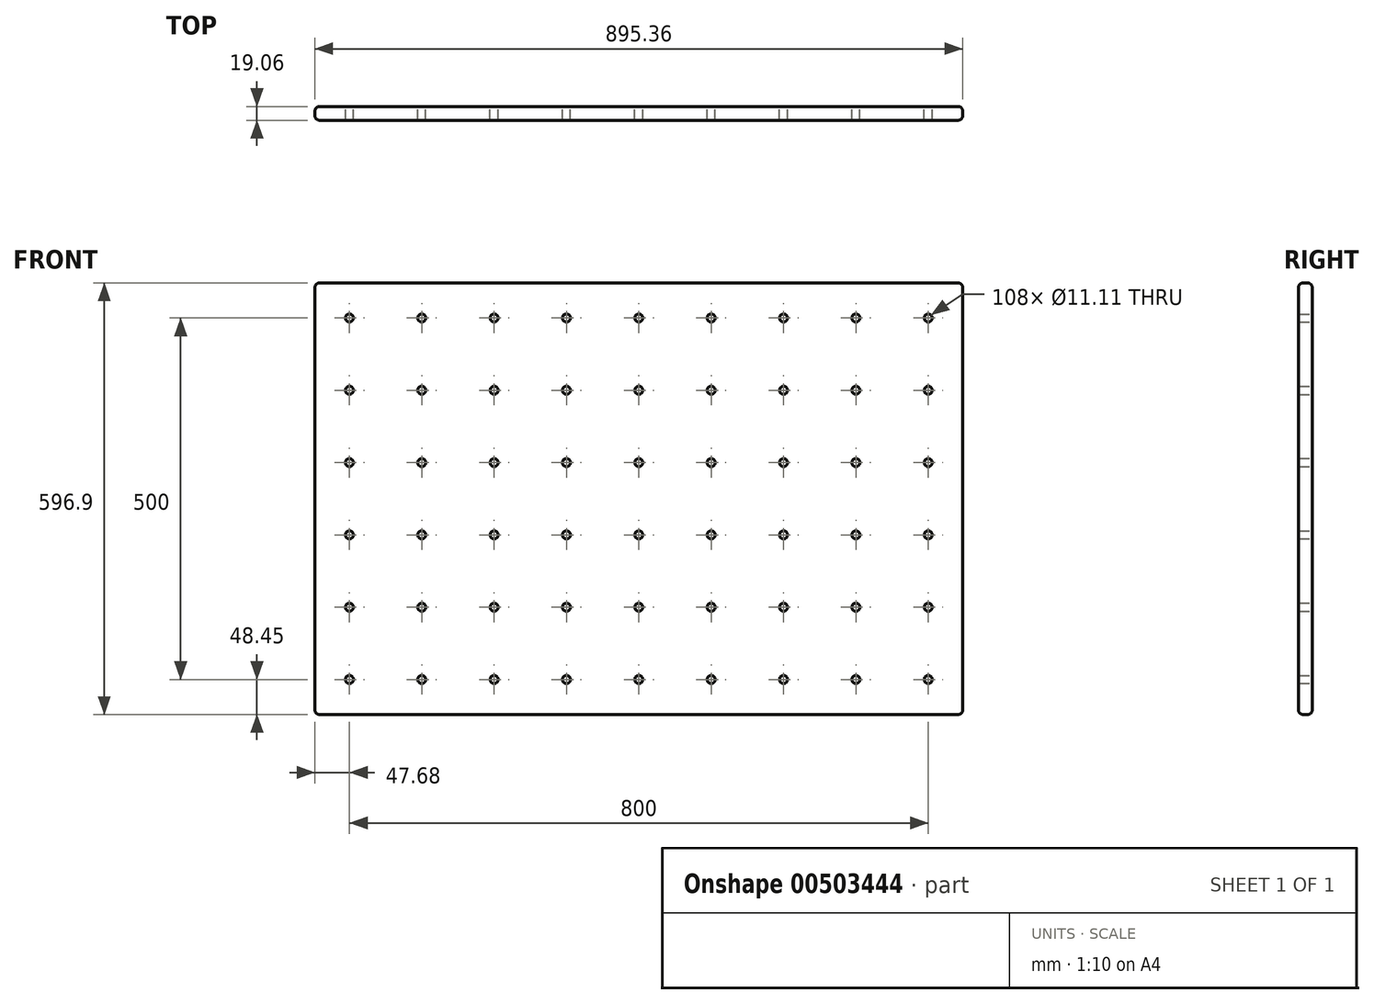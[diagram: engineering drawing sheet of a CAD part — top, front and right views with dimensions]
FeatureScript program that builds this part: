
annotation { "Feature Type Name" : "Feature", "Feature Type Description" : "" }
export const myFeature = defineFeature(function(context is Context, id is Id, definition is map)
    precondition{}
    {
        {
            var Q0;
            Q0=qCreatedBy(makeId("Front.planeOp"),FACE);
            var sketch = newSketch(context, id + "F0", { "sketchPlane" : qUnion([Q0])});
            skLineSegment(sketch, "E0.bottom", {"start": v(-447.68, 298.45) * mm, "end": v(447.68, 298.45) * mm});
            skLineSegment(sketch, "E0.top", {"start": v(-447.68, -298.45) * mm, "end": v(447.67, -298.45) * mm});
            skLineSegment(sketch, "E0.left", {"start": v(-447.68, 298.45) * mm, "end": v(-447.68, -298.45) * mm});
            skLineSegment(sketch, "E0.right", {"start": v(447.68, 298.45) * mm, "end": v(447.67, -298.45) * mm});
            skCircle(sketch, "E1", {"center": v(400, -250) * mm, "radius": 5.56 * mm});
            skCircle(sketch, "E2.0.1.0", {"center": v(400, -150) * mm, "radius": 5.56 * mm});
            skCircle(sketch, "E2.0.2.0", {"center": v(400, -50) * mm, "radius": 5.56 * mm});
            skCircle(sketch, "E2.0.3.0", {"center": v(400, 50) * mm, "radius": 5.56 * mm});
            skCircle(sketch, "E2.0.4.0", {"center": v(400, 150) * mm, "radius": 5.56 * mm});
            skCircle(sketch, "E2.0.5.0", {"center": v(400, 250) * mm, "radius": 5.56 * mm});
            skCircle(sketch, "E2.1.0.0", {"center": v(300, -250) * mm, "radius": 5.56 * mm});
            skCircle(sketch, "E2.1.1.0", {"center": v(300, -150) * mm, "radius": 5.56 * mm});
            skCircle(sketch, "E2.1.2.0", {"center": v(300, -50) * mm, "radius": 5.56 * mm});
            skCircle(sketch, "E2.1.3.0", {"center": v(300, 50) * mm, "radius": 5.56 * mm});
            skCircle(sketch, "E2.1.4.0", {"center": v(300, 150) * mm, "radius": 5.56 * mm});
            skCircle(sketch, "E2.1.5.0", {"center": v(300, 250) * mm, "radius": 5.56 * mm});
            skCircle(sketch, "E2.2.0.0", {"center": v(200, -250) * mm, "radius": 5.56 * mm});
            skCircle(sketch, "E2.2.1.0", {"center": v(200, -150) * mm, "radius": 5.56 * mm});
            skCircle(sketch, "E2.2.2.0", {"center": v(200, -50) * mm, "radius": 5.56 * mm});
            skCircle(sketch, "E2.2.3.0", {"center": v(200, 50) * mm, "radius": 5.56 * mm});
            skCircle(sketch, "E2.2.4.0", {"center": v(200, 150) * mm, "radius": 5.56 * mm});
            skCircle(sketch, "E2.2.5.0", {"center": v(200, 250) * mm, "radius": 5.56 * mm});
            skCircle(sketch, "E2.3.0.0", {"center": v(100, -250) * mm, "radius": 5.56 * mm});
            skCircle(sketch, "E2.3.1.0", {"center": v(100, -150) * mm, "radius": 5.56 * mm});
            skCircle(sketch, "E2.3.2.0", {"center": v(100, -50) * mm, "radius": 5.56 * mm});
            skCircle(sketch, "E2.3.3.0", {"center": v(100, 50) * mm, "radius": 5.56 * mm});
            skCircle(sketch, "E2.3.4.0", {"center": v(100, 150) * mm, "radius": 5.56 * mm});
            skCircle(sketch, "E2.3.5.0", {"center": v(100, 250) * mm, "radius": 5.56 * mm});
            skCircle(sketch, "E2.4.0.0", {"center": v(0, -250) * mm, "radius": 5.56 * mm});
            skCircle(sketch, "E2.4.1.0", {"center": v(0, -150) * mm, "radius": 5.56 * mm});
            skCircle(sketch, "E2.4.2.0", {"center": v(0, -50) * mm, "radius": 5.56 * mm});
            skCircle(sketch, "E2.4.3.0", {"center": v(0, 50) * mm, "radius": 5.56 * mm});
            skCircle(sketch, "E2.4.4.0", {"center": v(0, 150) * mm, "radius": 5.56 * mm});
            skCircle(sketch, "E2.4.5.0", {"center": v(0, 250) * mm, "radius": 5.56 * mm});
            skCircle(sketch, "E2.5.0.0", {"center": v(-100, -250) * mm, "radius": 5.56 * mm});
            skCircle(sketch, "E2.5.1.0", {"center": v(-100, -150) * mm, "radius": 5.56 * mm});
            skCircle(sketch, "E2.5.2.0", {"center": v(-100, -50) * mm, "radius": 5.56 * mm});
            skCircle(sketch, "E2.5.3.0", {"center": v(-100, 50) * mm, "radius": 5.56 * mm});
            skCircle(sketch, "E2.5.4.0", {"center": v(-100, 150) * mm, "radius": 5.56 * mm});
            skCircle(sketch, "E2.5.5.0", {"center": v(-100, 250) * mm, "radius": 5.56 * mm});
            skCircle(sketch, "E2.6.0.0", {"center": v(-200, -250) * mm, "radius": 5.56 * mm});
            skCircle(sketch, "E2.6.1.0", {"center": v(-200, -150) * mm, "radius": 5.56 * mm});
            skCircle(sketch, "E2.6.2.0", {"center": v(-200, -50) * mm, "radius": 5.56 * mm});
            skCircle(sketch, "E2.6.3.0", {"center": v(-200, 50) * mm, "radius": 5.56 * mm});
            skCircle(sketch, "E2.6.4.0", {"center": v(-200, 150) * mm, "radius": 5.56 * mm});
            skCircle(sketch, "E2.6.5.0", {"center": v(-200, 250) * mm, "radius": 5.56 * mm});
            skCircle(sketch, "E2.7.0.0", {"center": v(-300, -250) * mm, "radius": 5.56 * mm});
            skCircle(sketch, "E2.7.1.0", {"center": v(-300, -150) * mm, "radius": 5.56 * mm});
            skCircle(sketch, "E2.7.2.0", {"center": v(-300, -50) * mm, "radius": 5.56 * mm});
            skCircle(sketch, "E2.7.3.0", {"center": v(-300, 50) * mm, "radius": 5.56 * mm});
            skCircle(sketch, "E2.7.4.0", {"center": v(-300, 150) * mm, "radius": 5.56 * mm});
            skCircle(sketch, "E2.7.5.0", {"center": v(-300, 250) * mm, "radius": 5.56 * mm});
            skCircle(sketch, "E2.8.0.0", {"center": v(-400, -250) * mm, "radius": 5.56 * mm});
            skCircle(sketch, "E2.8.1.0", {"center": v(-400, -150) * mm, "radius": 5.56 * mm});
            skCircle(sketch, "E2.8.2.0", {"center": v(-400, -50) * mm, "radius": 5.56 * mm});
            skCircle(sketch, "E2.8.3.0", {"center": v(-400, 50) * mm, "radius": 5.56 * mm});
            skCircle(sketch, "E2.8.4.0", {"center": v(-400, 150) * mm, "radius": 5.56 * mm});
            skCircle(sketch, "E2.8.5.0", {"center": v(-400, 250) * mm, "radius": 5.56 * mm});
            skLineSegment(sketch, "E2.direction1", {"start": v(400, -250) * mm, "end": v(300, -250) * mm, "construction": true});
            skLineSegment(sketch, "E2.direction2", {"start": v(400, -250) * mm, "end": v(400, -150) * mm, "construction": true});
            skSolve(sketch);
        }
        {
            var Q0;
            Q0=makeQuery(id+"F0.imprint","IMPRINT",FACE,{"disambiguationData":[TD([[makeQuery(id+"F0.imprint","IMPRINT",EDGE,{"derivedFrom":sQuery(id+"F0.wireOp",EDGE,"E0.bottom")}),-1.0]])]});
            extrude(context, id + "F1", {"entities" : qUnion([Q0]), "depth" : 19.05 * mm, "symmetric" : true});
        }
        {
            var Q0;
            Q0=makeQuery(id+"F1.opExtrude","SWEPT_EDGE",EDGE,{"disambiguationData":[OSD([sQuery(id+"F0.wireOp",EDGE,"E0.bottom"),sQuery(id+"F0.wireOp",EDGE,"E0.left")])]});
            var Q1;
            Q1=makeQuery(id+"F1.opExtrude","CAP_EDGE",EDGE,{"disambiguationData":[OSD([sQuery(id+"F0.wireOp",EDGE,"E0.bottom")])],"isStart":true});
            var Q2;
            Q2=makeQuery(id+"F1.opExtrude","CAP_EDGE",EDGE,{"disambiguationData":[OSD([sQuery(id+"F0.wireOp",EDGE,"E0.left")])],"isStart":true});
            var Q3;
            Q3=makeQuery(id+"F1.opExtrude","CAP_EDGE",EDGE,{"disambiguationData":[OSD([sQuery(id+"F0.wireOp",EDGE,"E0.left")])],"isStart":false});
            var Q4;
            Q4=makeQuery(id+"F1.opExtrude","SWEPT_EDGE",EDGE,{"disambiguationData":[OSD([sQuery(id+"F0.wireOp",EDGE,"E0.bottom"),sQuery(id+"F0.wireOp",EDGE,"E0.right")])]});
            var Q5;
            Q5=makeQuery(id+"F1.opExtrude","CAP_EDGE",EDGE,{"disambiguationData":[OSD([sQuery(id+"F0.wireOp",EDGE,"E0.bottom")])],"isStart":false});
            var Q6;
            Q6=makeQuery(id+"F1.opExtrude","CAP_EDGE",EDGE,{"disambiguationData":[OSD([sQuery(id+"F0.wireOp",EDGE,"E0.right")])],"isStart":false});
            var Q7;
            Q7=makeQuery(id+"F1.opExtrude","CAP_EDGE",EDGE,{"disambiguationData":[OSD([sQuery(id+"F0.wireOp",EDGE,"E0.top")])],"isStart":false});
            var Q8;
            Q8=makeQuery(id+"F1.opExtrude","SWEPT_EDGE",EDGE,{"disambiguationData":[OSD([sQuery(id+"F0.wireOp",EDGE,"E0.top"),sQuery(id+"F0.wireOp",EDGE,"E0.left")])]});
            var Q9;
            Q9=makeQuery(id+"F1.opExtrude","CAP_EDGE",EDGE,{"disambiguationData":[OSD([sQuery(id+"F0.wireOp",EDGE,"E0.top")])],"isStart":true});
            var Q10;
            Q10=makeQuery(id+"F1.opExtrude","SWEPT_EDGE",EDGE,{"disambiguationData":[OSD([sQuery(id+"F0.wireOp",EDGE,"E0.top"),sQuery(id+"F0.wireOp",EDGE,"E0.right")])]});
            var Q11;
            Q11=makeQuery(id+"F1.opExtrude","CAP_EDGE",EDGE,{"disambiguationData":[OSD([sQuery(id+"F0.wireOp",EDGE,"E0.right")])],"isStart":true});
            fillet(context, id + "F2", {"entities" : qUnion([Q0, Q1, Q2, Q3, Q4, Q5, Q6, Q7, Q8, Q9, Q10, Q11]), "radius" : 6.35 * mm, "tangentPropagation" : true, "allowEdgeOverflow" : false});
        }
    });
